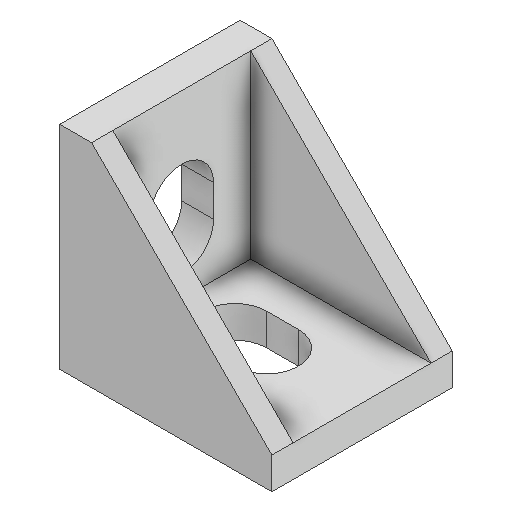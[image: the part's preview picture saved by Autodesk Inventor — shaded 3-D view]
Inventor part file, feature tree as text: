
AUTODESK INVENTOR PART (.ipt)
format: ipt  version: 2024.1 (Build 281209000, 209)  size: 154,112 bytes
history: native  units: in
note: dims shown in document units (in); Inventor stores cm internally (conversion verified against a paired STEP export)
features: extrude x3, plane x1, pattern_circular x1
ambient origin geometry x8: Origin, YZ Plane, XZ Plane, XY Plane, X Axis, Y Axis, Z Axis, Center Point
bodies: Solid1 (feature_tree)
feature tree (5):
  extrude  "Extrusion1"  Depth=0.7874in
  plane  "Work Plane1"
  extrude  "Extrusion2"  Depth=0.1181in
  extrude  "Extrusion3"  Depth=0.6693in TaperAngle=0.0deg
  pattern_circular  "Circular Pattern2"  [2 undecoded]
note: 2 required parameter values undecoded (feature->parameter linkage not recoverable at this tier; creation-order binding heuristic only, values carry confidence <= 0.55)
